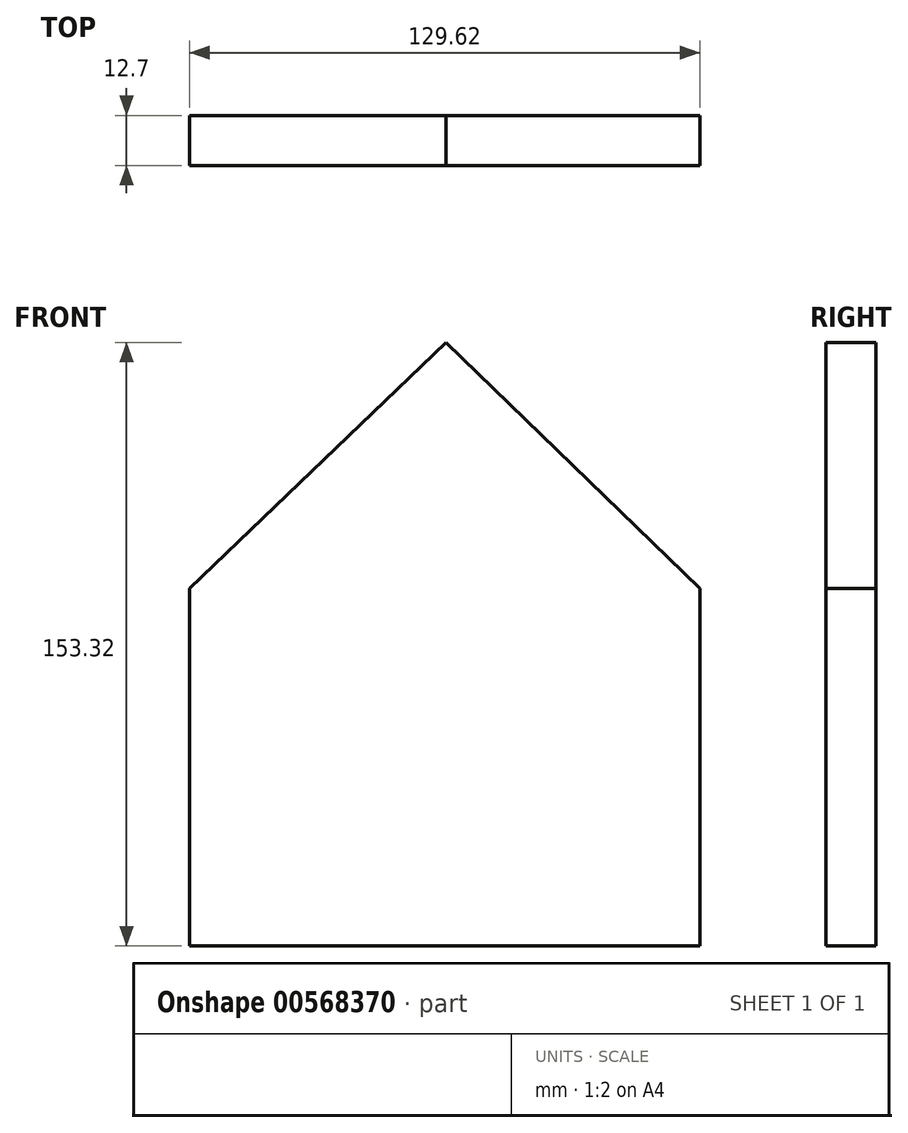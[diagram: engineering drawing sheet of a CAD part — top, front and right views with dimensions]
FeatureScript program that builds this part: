
annotation { "Feature Type Name" : "Feature", "Feature Type Description" : "" }
export const myFeature = defineFeature(function(context is Context, id is Id, definition is map)
    precondition{}
    {
        {
            var Q0;
            Q0=qCreatedBy(makeId("Front.planeOp"),FACE);
            var sketch = newSketch(context, id + "F0", { "sketchPlane" : qUnion([Q0])});
            skLineSegment(sketch, "E0.bottom", {"start": v(-65.1, 39.23) * mm, "end": v(64.52, 39.23) * mm});
            skLineSegment(sketch, "E0.top", {"start": v(-65.1, -51.57) * mm, "end": v(64.52, -51.57) * mm});
            skLineSegment(sketch, "E0.left", {"start": v(-65.1, 39.23) * mm, "end": v(-65.1, -51.57) * mm});
            skLineSegment(sketch, "E0.right", {"start": v(64.52, 39.23) * mm, "end": v(64.52, -51.57) * mm});
            skLineSegment(sketch, "E1", {"start": v(-65.1, 39.23) * mm, "end": v(0, 101.75) * mm});
            skLineSegment(sketch, "E2", {"start": v(0, 101.75) * mm, "end": v(64.52, 39.23) * mm});
            skSolve(sketch);
        }
        {
            var Q0;
            Q0=makeQuery(id+"F0.imprint","IMPRINT",FACE,{"disambiguationData":[TD([[makeQuery(id+"F0.imprint","IMPRINT",EDGE,{"derivedFrom":sQuery(id+"F0.wireOp",EDGE,"E0.bottom")}),-1.0]])]});
            var Q1;
            Q1=makeQuery(id+"F0.imprint","IMPRINT",FACE,{"disambiguationData":[TD([[makeQuery(id+"F0.imprint","IMPRINT",EDGE,{"derivedFrom":sQuery(id+"F0.wireOp",EDGE,"E0.bottom")}),1.0]])]});
            extrude(context, id + "F1", {"entities" : qUnion([Q0, Q1]), "depth" : 12.7 * mm, "offsetDistance" : 25.4 * mm});
        }
    });
